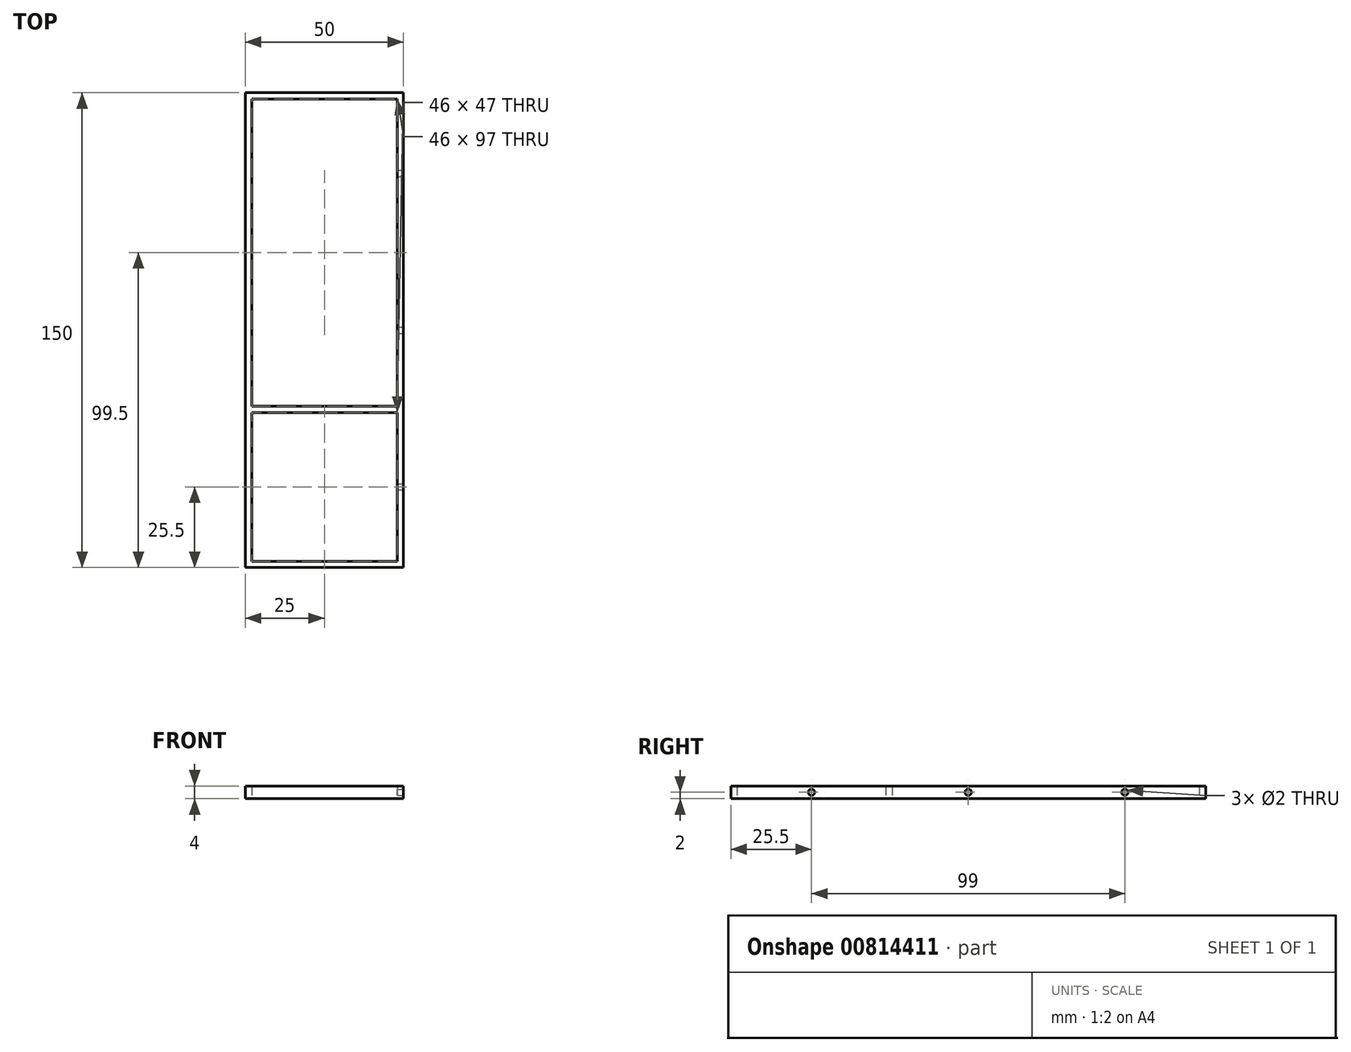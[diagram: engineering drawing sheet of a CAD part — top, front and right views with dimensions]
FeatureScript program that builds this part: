
annotation { "Feature Type Name" : "Feature", "Feature Type Description" : "" }
export const myFeature = defineFeature(function(context is Context, id is Id, definition is map)
    precondition{}
    {
        {
            var Q0;
            Q0=qCreatedBy(makeId("Top.planeOp"),FACE);
            var sketch = newSketch(context, id + "F0", { "sketchPlane" : qUnion([Q0])});
            skLineSegment(sketch, "E0.bottom", {"start": v(-25, 75) * mm, "end": v(25, 75) * mm});
            skLineSegment(sketch, "E0.top", {"start": v(-25, -75) * mm, "end": v(25, -75) * mm});
            skLineSegment(sketch, "E0.left", {"start": v(-25, 75) * mm, "end": v(-25, -75) * mm});
            skLineSegment(sketch, "E0.right", {"start": v(25, 75) * mm, "end": v(25, -75) * mm});
            skPoint(sketch, "E0.middle", {"position": v(0, 0) * mm});
            skLineSegment(sketch, "E1.bottom", {"start": v(-23, -73) * mm, "end": v(23, -73) * mm});
            skLineSegment(sketch, "E1.top", {"start": v(-23, -26) * mm, "end": v(23, -26) * mm});
            skLineSegment(sketch, "E1.left", {"start": v(-23, -73) * mm, "end": v(-23, -26) * mm});
            skLineSegment(sketch, "E1.right", {"start": v(23, -73) * mm, "end": v(23, -26) * mm});
            skPoint(sketch, "E1.middle", {"position": v(0, -49.5) * mm});
            skLineSegment(sketch, "E2.bottom", {"start": v(-23, 73) * mm, "end": v(23, 73) * mm});
            skLineSegment(sketch, "E2.top", {"start": v(-23, -24) * mm, "end": v(23, -24) * mm});
            skLineSegment(sketch, "E2.left", {"start": v(-23, 73) * mm, "end": v(-23, -24) * mm});
            skLineSegment(sketch, "E2.right", {"start": v(23, 73) * mm, "end": v(23, -24) * mm});
            skPoint(sketch, "E2.middle", {"position": v(0, 24.5) * mm});
            skSolve(sketch);
        }
        {
            var Q0;
            Q0 = qSketchRegion(id + "F0", true);
            extrude(context, id + "F1", {"entities" : qUnion([Q0]), "depth" : 4 * mm, "offsetDistance" : 25 * mm});
        }
        {
            var Q0;
            Q0=makeQuery(id+"F1.opExtrude","SWEPT_FACE",FACE,{"disambiguationData":[OSD([sQuery(id+"F0.wireOp",EDGE,"E0.right")])]});
            var sketch = newSketch(context, id + "F2", { "sketchPlane" : qUnion([Q0])});
            skCircle(sketch, "E3", {"center": v(-49.5, 2) * mm, "radius": 1 * mm});
            skCircle(sketch, "E4", {"center": v(0, 2) * mm, "radius": 1 * mm});
            skCircle(sketch, "E5", {"center": v(49.5, 2) * mm, "radius": 1 * mm});
            skPoint(sketch, "E6", {"position": v(-24, 4) * mm});
            skLineSegment(sketch, "E7", {"start": v(-24, 4) * mm, "end": v(-24, 0) * mm});
            skSolve(sketch);
        }
        {
            var Q0;
            Q0 = qSketchRegion(id + "F2", true);
            extrude(context, id + "F3", {"entities" : qUnion([Q0]), "operationType" : NewBodyOperationType.REMOVE, "oppositeDirection" : true, "depth" : 25 * mm, "offsetDistance" : 25 * mm});
        }
    });
